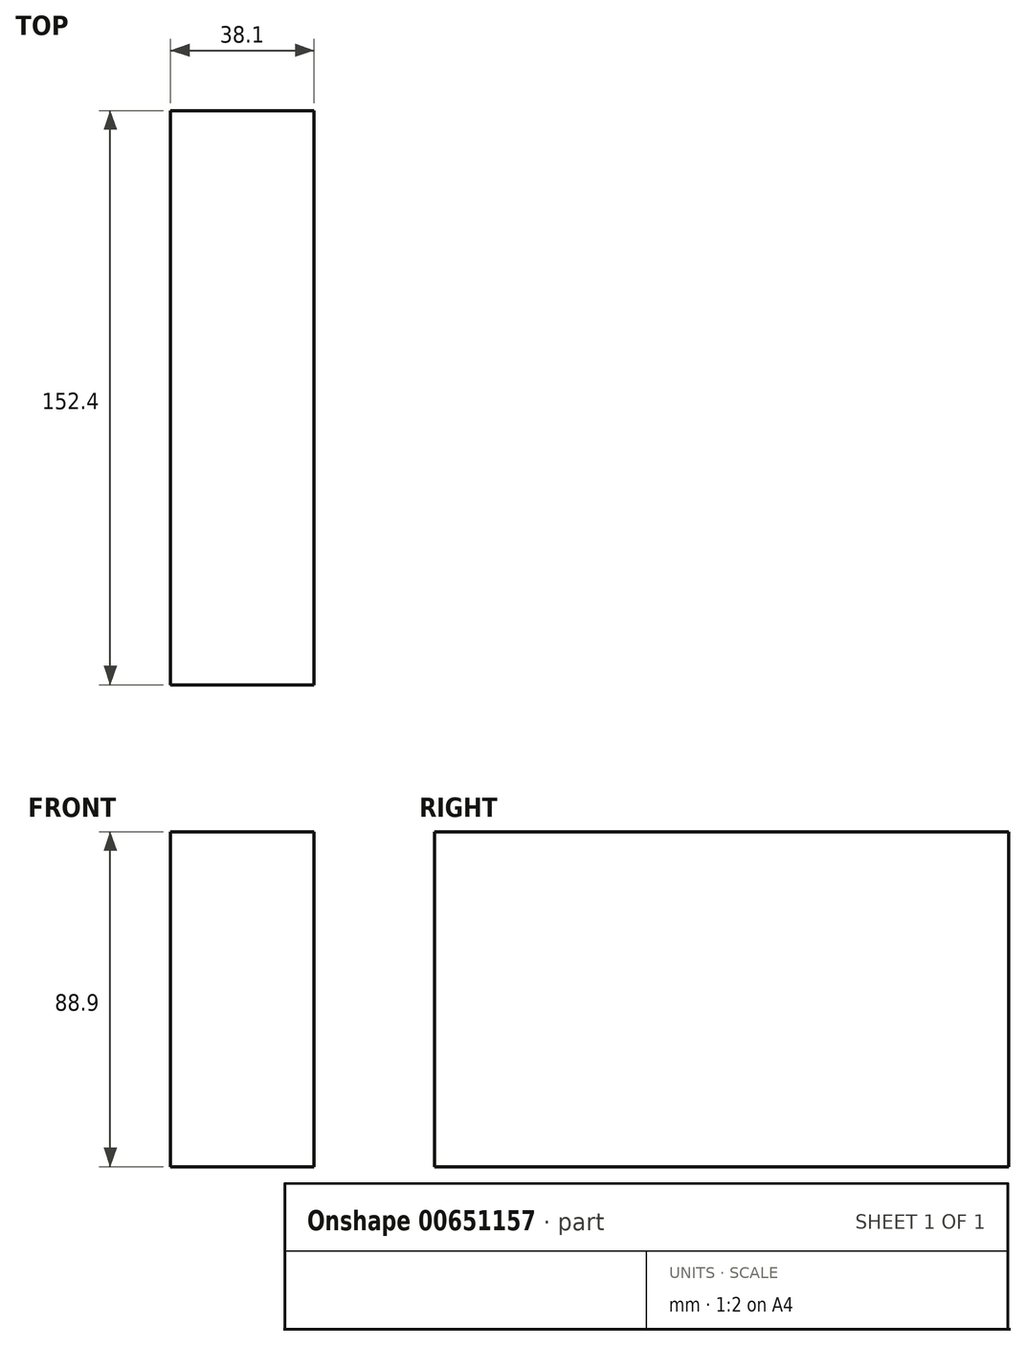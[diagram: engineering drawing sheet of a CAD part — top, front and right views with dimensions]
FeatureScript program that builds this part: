
annotation { "Feature Type Name" : "Feature", "Feature Type Description" : "" }
export const myFeature = defineFeature(function(context is Context, id is Id, definition is map)
    precondition{}
    {
        {
            var Q0;
            Q0=qCreatedBy(makeId("Front.planeOp"),FACE);
            var sketch = newSketch(context, id + "F0", { "sketchPlane" : qUnion([Q0])});
            skLineSegment(sketch, "E0.bottom", {"start": v(-19.05, 44.45) * mm, "end": v(19.05, 44.45) * mm});
            skLineSegment(sketch, "E0.top", {"start": v(-19.05, -44.45) * mm, "end": v(19.05, -44.45) * mm});
            skLineSegment(sketch, "E0.left", {"start": v(-19.05, 44.45) * mm, "end": v(-19.05, -44.45) * mm});
            skLineSegment(sketch, "E0.right", {"start": v(19.05, 44.45) * mm, "end": v(19.05, -44.45) * mm});
            skPoint(sketch, "E0.middle", {"position": v(0, 0) * mm});
            skSolve(sketch);
        }
        {
            var Q0;
            Q0 = qSketchRegion(id + "F0", true);
            extrude(context, id + "F1", {"entities" : qUnion([Q0]), "depth" : 152.4 * mm, "offsetDistance" : 25.4 * mm});
        }
    });
